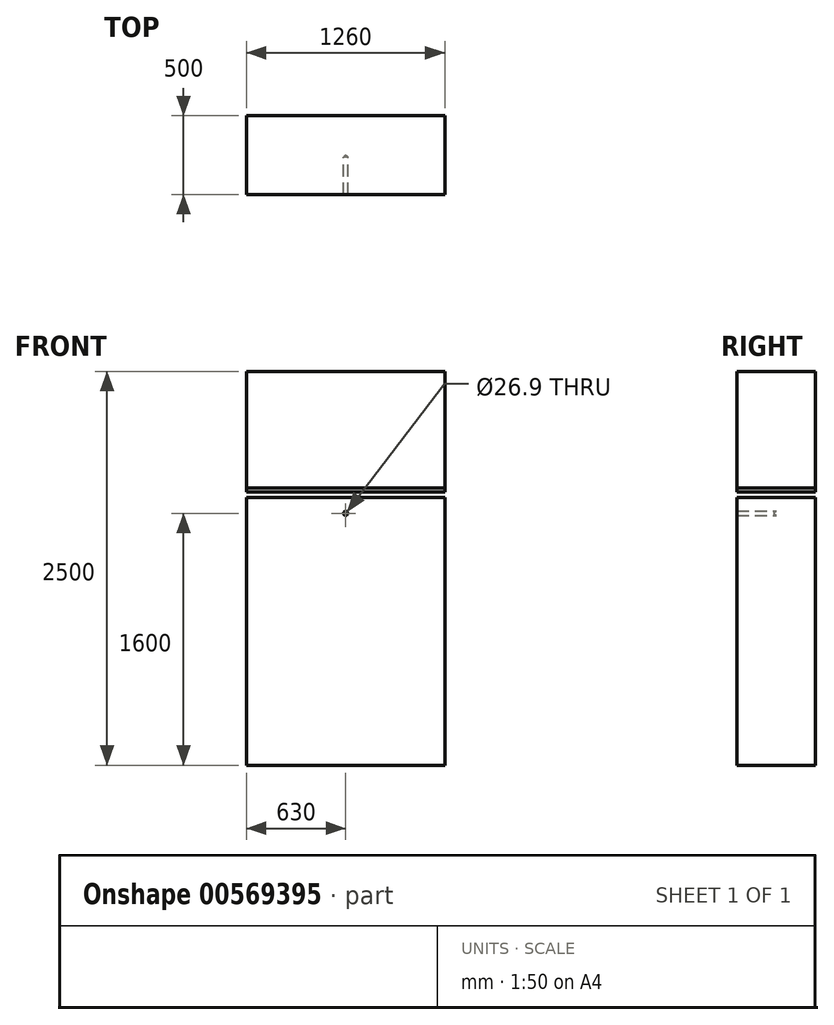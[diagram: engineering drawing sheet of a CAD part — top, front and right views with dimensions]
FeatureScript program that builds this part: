
annotation { "Feature Type Name" : "Feature", "Feature Type Description" : "" }
export const myFeature = defineFeature(function(context is Context, id is Id, definition is map)
    precondition{}
    {
        {
            var Q0;
            Q0=qCreatedBy(makeId("Top.planeOp"),FACE);
            var sketch = newSketch(context, id + "F0", { "sketchPlane" : qUnion([Q0])});
            skLineSegment(sketch, "E0", {"start": v(-630, -610) * mm, "end": v(-630, 0) * mm});
            skLineSegment(sketch, "E1", {"start": v(-630, 0) * mm, "end": v(630, 0) * mm});
            skLineSegment(sketch, "E2", {"start": v(630, 0) * mm, "end": v(630, -610) * mm});
            skLineSegment(sketch, "E3", {"start": v(0, 0) * mm, "end": v(0, -191.1) * mm, "construction": true});
            skSolve(sketch);
        }
        {
            var Q0;
            Q0 = qConstructionFilter(qBodyType(qCreatedBy(id + "F0" ,EDGE), BodyType.WIRE), ConstructionObject.NO);
            extrude(context, id + "F1", {"bodyType" : ToolBodyType.SURFACE, "surfaceEntities" : qUnion([Q0]), "depth" : 2500 * mm, "offsetDistance" : 25 * mm});
        }
        {
            var Q0;
            Q0=qCreatedBy(makeId("Top.planeOp"),FACE);
            cPlane(context, id + "F2", {"entities" : qUnion([Q0]), "cplaneType" : CPlaneType.OFFSET, "offset" : 1600 * mm, "width" : 150 * mm, "height" : 150 * mm});
        }
        {
            var Q0;
            Q0=makeQuery(id+"F1.opExtrude","SWEPT_FACE",FACE,{"disambiguationData":[OSD([sQuery(id+"F0.wireOp",EDGE,"E1")])]});
            cPlane(context, id + "F3", {"entities" : qUnion([Q0]), "cplaneType" : CPlaneType.OFFSET, "offset" : 250 * mm, "width" : 150 * mm, "height" : 150 * mm});
        }
        {
            var Q0;
            Q0=qCreatedBy(id+"F3.planeOp",FACE);
            var sketch = newSketch(context, id + "F4", { "sketchPlane" : qUnion([Q0])});
            skLineSegment(sketch, "E4", {"start": v(0, 0) * mm, "end": v(0, 1600) * mm, "construction": true});
            skLineSegment(sketch, "E5", {"start": v(0, 1600) * mm, "end": v(-470, 1600) * mm});
            skLineSegment(sketch, "E6", {"start": v(-500, 1630) * mm, "end": v(-500, 1720) * mm});
            skPoint(sketch, "E7.visualSharp", {"position": v(-500, 1600) * mm});
            skArc(sketch, "E7.filletArc", {"start": v(-500, 1630) * mm, "mid": v(-491.21, 1608.79) * mm, "end": v(-470, 1600) * mm});
            skLineSegment(sketch, "E8.MirrorCS", {"start": v(500, 1630) * mm, "end": v(500, 1720) * mm});
            skArc(sketch, "E9.MirrorCS", {"start": v(500, 1630) * mm, "mid": v(491.21, 1608.79) * mm, "end": v(470, 1600) * mm});
            skLineSegment(sketch, "E10.MirrorCS", {"start": v(0, 1600) * mm, "end": v(470, 1600) * mm});
            skSolve(sketch);
        }
        {
            var Q0;
            Q0=qCreatedBy(id+"F2.planeOp",FACE);
            var sketch = newSketch(context, id + "F5", { "sketchPlane" : qUnion([Q0])});
            skLineSegment(sketch, "E11", {"start": v(0, 0) * mm, "end": v(0, -250) * mm});
            skSolve(sketch);
        }
        {
            var Q0;
            Q0=qCreatedBy(id+"F2.planeOp",FACE);
            cPlane(context, id + "F6", {"entities" : qUnion([Q0]), "cplaneType" : CPlaneType.OFFSET, "offset" : 100 * mm, "width" : 150 * mm, "height" : 150 * mm});
        }
        {
            var Q0;
            Q0=qCreatedBy(makeId("Right.planeOp"),FACE);
            var sketch = newSketch(context, id + "F7", { "sketchPlane" : qUnion([Q0])});
            skCircle(sketch, "E12", {"center": v(-250, 1600) * mm, "radius": 13.45 * mm});
            skSolve(sketch);
        }
        {
            var Q0;
            Q0=makeQuery(id+"F7.imprint","IMPRINT",FACE,{"disambiguationData":[TD([[makeQuery(id+"F7.imprint","IMPRINT",EDGE,{"derivedFrom":sQuery(id+"F7.wireOp",EDGE,"E12")}),1.0]])]});
            var Q1;
            Q1=sQuery(id+"F4.wireOp",EDGE,"E5");
            var Q2;
            Q2=sQuery(id+"F4.wireOp",EDGE,"E7.filletArc");
            var Q3;
            Q3=sQuery(id+"F4.wireOp",EDGE,"E6");
            sweep(context, id + "F8", {"profiles" : qUnion([Q0]), "path" : qUnion([Q1, Q2, Q3])});
        }
        {
            var Q0;
            Q0 = qSketchRegion(id + "F7", true);
            var Q1;
            Q1=sQuery(id+"F4.wireOp",EDGE,"E10.MirrorCS");
            var Q2;
            Q2=sQuery(id+"F4.wireOp",EDGE,"E9.MirrorCS");
            var Q3;
            Q3=sQuery(id+"F4.wireOp",EDGE,"E8.MirrorCS");
            sweep(context, id + "F9", {"operationType" : NewBodyOperationType.ADD, "profiles" : qUnion([Q0]), "path" : qUnion([Q1, Q2, Q3])});
        }
        {
            var Q0;
            Q0=makeQuery(id+"F1.opExtrude","SWEPT_FACE",FACE,{"disambiguationData":[OSD([sQuery(id+"F0.wireOp",EDGE,"E1")])]});
            var sketch = newSketch(context, id + "F10", { "sketchPlane" : qUnion([Q0])});
            skCircle(sketch, "E13", {"center": v(-500, 1720) * mm, "radius": 13.45 * mm});
            skCircle(sketch, "E14", {"center": v(0, 1600) * mm, "radius": 13.45 * mm});
            skLineSegment(sketch, "E15", {"start": v(0, 2064.15) * mm, "end": v(0, 1514.23) * mm, "construction": true});
            skCircle(sketch, "E16.MirrorC", {"center": v(500, 1720) * mm, "radius": 13.45 * mm});
            skSolve(sketch);
        }
        {
            var Q0;
            Q0=makeQuery(id+"F10.imprint","IMPRINT",FACE,{"disambiguationData":[TD([[makeQuery(id+"F10.imprint","IMPRINT",EDGE,{"derivedFrom":sQuery(id+"F10.wireOp",EDGE,"E14")}),1.0]])]});
            var Q1;
            Q1=makeQuery(id+"F8.opSweep","SWEPT_BODY",BODY,{"disambiguationData":[OSD([sQuery(id+"F4.wireOp",EDGE,"E6"),sQuery(id+"F7.wireOp",EDGE,"E12")])]});
            extrude(context, id + "F11", {"entities" : qUnion([Q0]), "operationType" : NewBodyOperationType.ADD, "endBound" : BoundingType.UP_TO_BODY, "depth" : 25 * mm, "endBoundEntityBody" : qUnion([Q1]), "offsetDistance" : 25 * mm});
        }
        {
            var Q0;
            Q0=makeQuery(id+"F10.imprint","IMPRINT",FACE,{"disambiguationData":[TD([[makeQuery(id+"F10.imprint","IMPRINT",EDGE,{"derivedFrom":sQuery(id+"F10.wireOp",EDGE,"E13")}),1.0]])]});
            var Q1;
            Q1=makeQuery(id+"F10.imprint","IMPRINT",FACE,{"disambiguationData":[TD([[makeQuery(id+"F10.imprint","IMPRINT",EDGE,{"derivedFrom":sQuery(id+"F10.wireOp",EDGE,"E16.MirrorC")}),-1.0]])]});
            extrude(context, id + "F12", {"entities" : qUnion([Q0, Q1]), "operationType" : NewBodyOperationType.ADD, "depth" : 500 * mm, "offsetDistance" : 25 * mm});
        }
        {
            var Q0;
            Q0=qCreatedBy(id+"F6.planeOp",FACE);
            var sketch = newSketch(context, id + "F13", { "sketchPlane" : qUnion([Q0])});
            skLineSegment(sketch, "E17.bottom", {"start": v(-630, 0) * mm, "end": v(630, 0) * mm});
            skLineSegment(sketch, "E17.top", {"start": v(-630, -500) * mm, "end": v(630, -500) * mm});
            skLineSegment(sketch, "E17.left", {"start": v(-630, 0) * mm, "end": v(-630, -500) * mm});
            skLineSegment(sketch, "E17.right", {"start": v(630, 0) * mm, "end": v(630, -500) * mm});
            skSolve(sketch);
        }
        {
            var Q0;
            Q0 = qSketchRegion(id + "F13", true);
            extrude(context, id + "F14", {"entities" : qUnion([Q0]), "depth" : 60 * mm, "offsetDistance" : 25 * mm});
        }
        {
            var Q0;
            Q0 = qSketchRegion(id + "F13", true);
            extrude(context, id + "F15", {"entities" : qUnion([Q0]), "operationType" : NewBodyOperationType.REMOVE, "depth" : 35 * mm, "offsetDistance" : 25 * mm});
        }
    });
